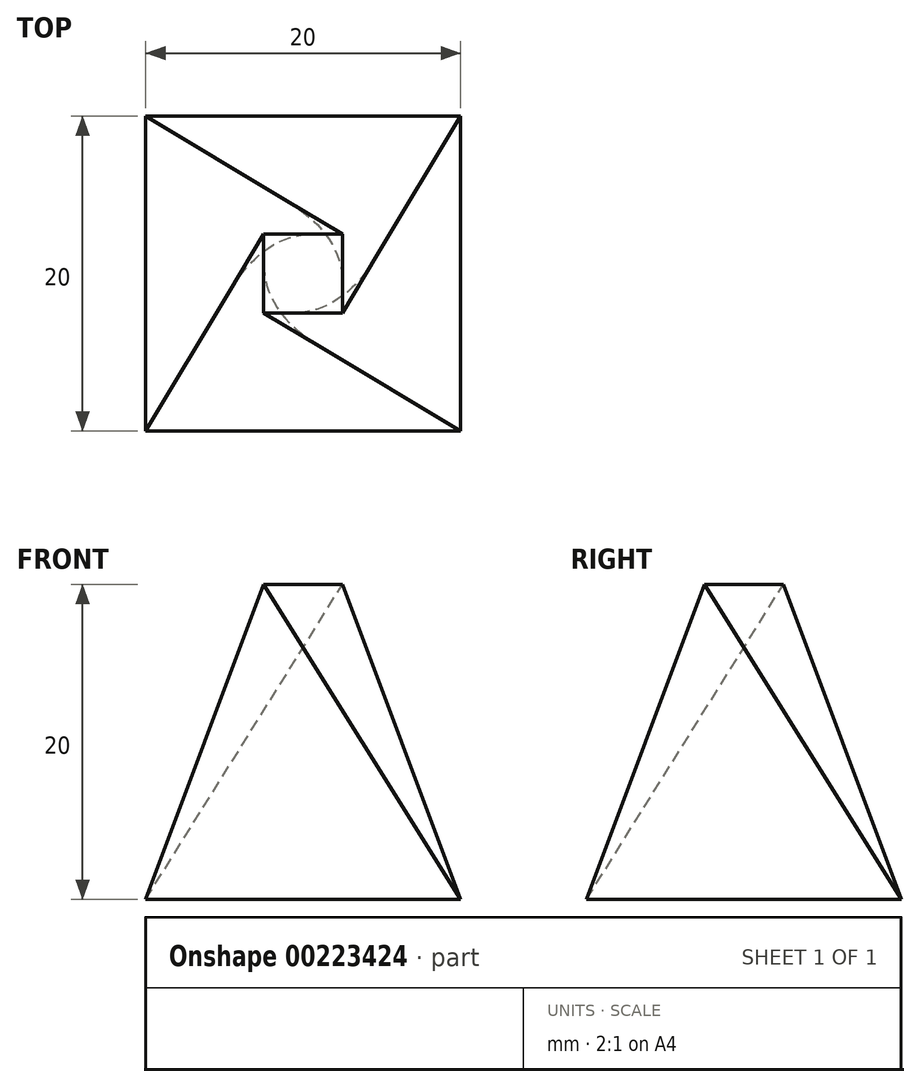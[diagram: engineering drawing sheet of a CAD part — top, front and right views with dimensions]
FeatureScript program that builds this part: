
annotation { "Feature Type Name" : "Feature", "Feature Type Description" : "" }
export const myFeature = defineFeature(function(context is Context, id is Id, definition is map)
    precondition{}
    {
        {
            var Q0;
            Q0=qCreatedBy(makeId("Top.planeOp"),FACE);
            var sketch = newSketch(context, id + "F0", { "sketchPlane" : qUnion([Q0])});
            skLineSegment(sketch, "E0.bottom", {"start": v(-10, 10) * mm, "end": v(10, 10) * mm});
            skLineSegment(sketch, "E0.top", {"start": v(-10, -10) * mm, "end": v(10, -10) * mm});
            skLineSegment(sketch, "E0.left", {"start": v(-10, 10) * mm, "end": v(-10, -10) * mm});
            skLineSegment(sketch, "E0.right", {"start": v(10, 10) * mm, "end": v(10, -10) * mm});
            skLineSegment(sketch, "E1", {"start": v(10, -10) * mm, "end": v(-10, 10) * mm, "construction": true});
            skSolve(sketch);
        }
        {
            var Q0;
            Q0=qCreatedBy(makeId("Top.planeOp"),FACE);
            cPlane(context, id + "F1", {"entities" : qUnion([Q0]), "cplaneType" : CPlaneType.OFFSET, "offset" : 20 * mm, "width" : 150 * mm, "height" : 150 * mm});
        }
        {
            var Q0;
            Q0=qCreatedBy(id+"F1.planeOp",FACE);
            var sketch = newSketch(context, id + "F2", { "sketchPlane" : qUnion([Q0])});
            skLineSegment(sketch, "E2.bottom", {"start": v(-2.5, 2.5) * mm, "end": v(2.5, 2.5) * mm});
            skLineSegment(sketch, "E2.top", {"start": v(-2.5, -2.5) * mm, "end": v(2.5, -2.5) * mm});
            skLineSegment(sketch, "E2.left", {"start": v(-2.5, 2.5) * mm, "end": v(-2.5, -2.5) * mm});
            skLineSegment(sketch, "E2.right", {"start": v(2.5, 2.5) * mm, "end": v(2.5, -2.5) * mm});
            skLineSegment(sketch, "E3", {"start": v(-2.5, 2.5) * mm, "end": v(2.5, -2.5) * mm, "construction": true});
            skSolve(sketch);
        }
        {
            var Q0;
            Q0 = qSketchRegion(id + "F0", true);
            var Q1;
            Q1 = qSketchRegion(id + "F2", true);
            var Q2;
            Q2=sQuery(id+"F0.wireOp",VERTEX,"E1.start");
            var Q3;
            Q3=sQuery(id+"F2.wireOp",VERTEX,"E2.left.end");
            loft(context, id + "F3", {"sheetProfilesArray" : [{ "sheetProfileEntities" : qUnion([Q0]) }, { "sheetProfileEntities" : qUnion([Q1]) }], "matchConnections" : true, "connections" : [{ "connectionEntities" : qUnion([Q2, Q3]), "connectionEdgeQueries" : qUnion([]), "connectionEdgeParameters" : [] }]});
        }
    });
